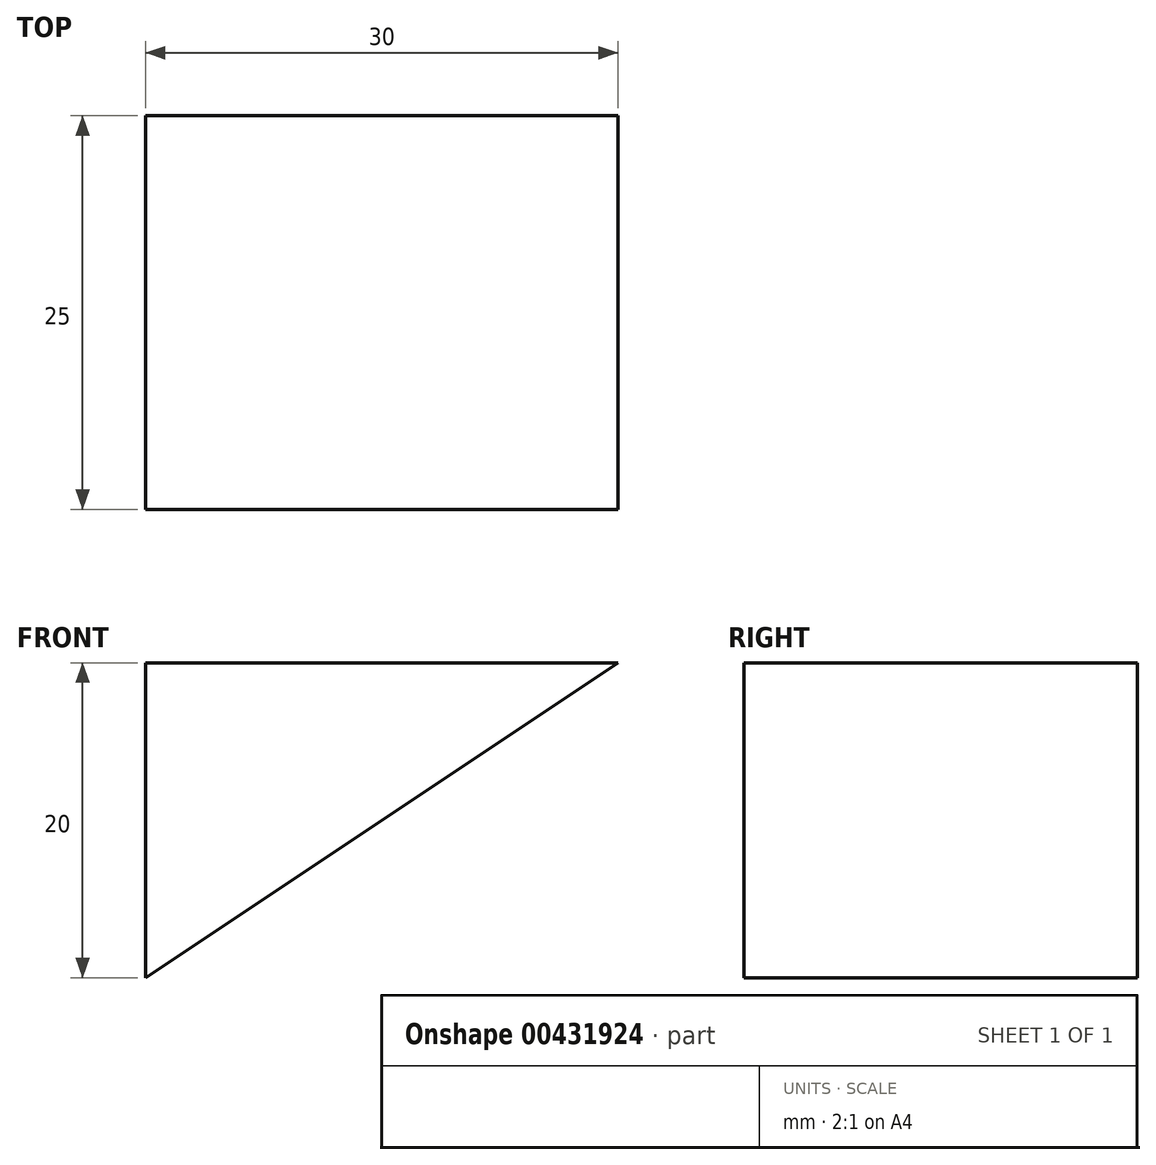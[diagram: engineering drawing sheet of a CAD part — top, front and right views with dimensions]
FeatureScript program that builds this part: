
annotation { "Feature Type Name" : "Feature", "Feature Type Description" : "" }
export const myFeature = defineFeature(function(context is Context, id is Id, definition is map)
    precondition{}
    {
        {
            var Q0;
            Q0=qCreatedBy(makeId("Front.planeOp"),FACE);
            var sketch = newSketch(context, id + "F0", { "sketchPlane" : qUnion([Q0])});
            skLineSegment(sketch, "E0.bottom", {"start": v(0, 0) * mm, "end": v(30, 0) * mm});
            skLineSegment(sketch, "E0.top", {"start": v(0, 20) * mm, "end": v(30, 20) * mm});
            skLineSegment(sketch, "E0.left", {"start": v(0, 0) * mm, "end": v(0, 20) * mm});
            skLineSegment(sketch, "E0.right", {"start": v(30, 0) * mm, "end": v(30, 20) * mm});
            skLineSegment(sketch, "E1", {"start": v(30, 20) * mm, "end": v(0, 0) * mm});
            skSolve(sketch);
        }
        {
            var Q0;
            Q0=makeQuery(id+"F0.imprint","IMPRINT",FACE,{"disambiguationData":[TD([[makeQuery(id+"F0.imprint","IMPRINT",EDGE,{"derivedFrom":sQuery(id+"F0.wireOp",EDGE,"E0.top")}),-1.0]])]});
            extrude(context, id + "F1", {"entities" : qUnion([Q0]), "depth" : 25 * mm});
        }
    });
